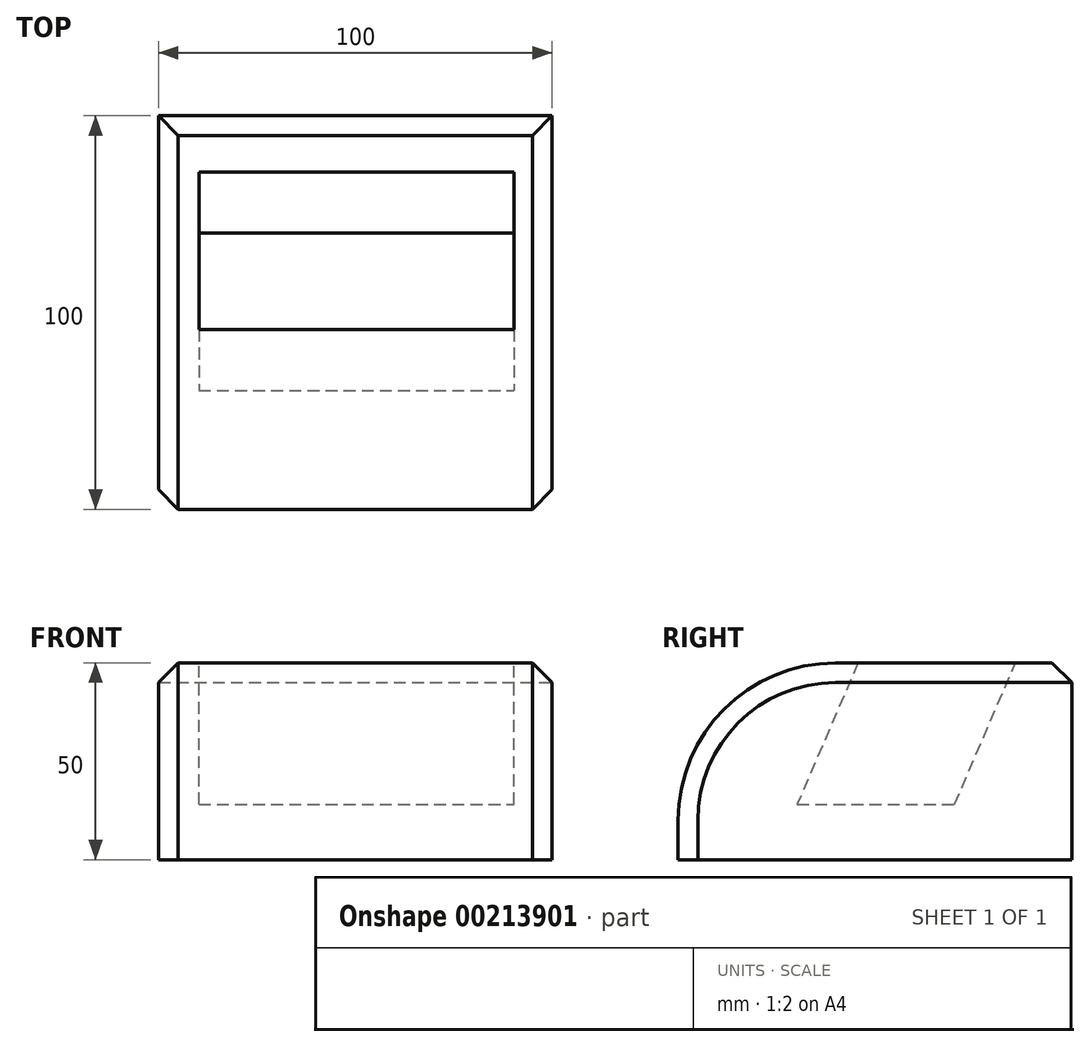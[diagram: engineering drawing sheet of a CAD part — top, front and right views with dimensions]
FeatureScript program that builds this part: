
annotation { "Feature Type Name" : "Feature", "Feature Type Description" : "" }
export const myFeature = defineFeature(function(context is Context, id is Id, definition is map)
    precondition{}
    {
        {
            var Q0;
            Q0=qCreatedBy(makeId("Front.planeOp"),FACE);
            var sketch = newSketch(context, id + "F0", { "sketchPlane" : qUnion([Q0])});
            skLineSegment(sketch, "E0.bottom", {"start": v(-50.24, 0.51) * mm, "end": v(49.76, 0.51) * mm});
            skLineSegment(sketch, "E0.top", {"start": v(-50.24, -49.49) * mm, "end": v(49.76, -49.49) * mm});
            skLineSegment(sketch, "E0.left", {"start": v(-50.24, 0.51) * mm, "end": v(-50.24, -49.49) * mm});
            skLineSegment(sketch, "E0.right", {"start": v(49.76, 0.51) * mm, "end": v(49.76, -49.49) * mm});
            skSolve(sketch);
        }
        {
            var Q0;
            Q0 = qSketchRegion(id + "F0", true);
            extrude(context, id + "F1", {"entities" : qUnion([Q0]), "endBound" : BoundingType.SYMMETRIC, "depth" : 100 * mm});
        }
        {
            var Q0;
            Q0=qCreatedBy(makeId("Right.planeOp"),FACE);
            var sketch = newSketch(context, id + "F2", { "sketchPlane" : qUnion([Q0])});
            skLineSegment(sketch, "E1", {"start": v(40, 10.51) * mm, "end": v(0, 10.51) * mm});
            skLineSegment(sketch, "E2", {"start": v(0, 10.51) * mm, "end": v(-19.77, -35.41) * mm});
            skLineSegment(sketch, "E3", {"start": v(-19.77, -35.41) * mm, "end": v(20.23, -35.41) * mm});
            skLineSegment(sketch, "E4", {"start": v(20.23, -35.41) * mm, "end": v(40, 10.51) * mm});
            skSolve(sketch);
        }
        {
            var Q0;
            Q0 = qSketchRegion(id + "F2", true);
            extrude(context, id + "F3", {"entities" : qUnion([Q0]), "operationType" : NewBodyOperationType.REMOVE, "endBound" : BoundingType.SYMMETRIC, "oppositeDirection" : true, "depth" : 80 * mm});
        }
        {
            var Q0;
            Q0=makeQuery(id+"F1.opExtrude","CAP_EDGE",EDGE,{"disambiguationData":[OSD([sQuery(id+"F0.wireOp",EDGE,"E0.bottom")])],"isStart":false});
            fillet(context, id + "F4", {"entities" : qUnion([Q0]), "radius" : 40 * mm, "tangentPropagation" : true, "allowEdgeOverflow" : false});
        }
        {
            var Q0;
            Q0=makeQuery(id+"F1.opExtrude","SWEPT_EDGE",EDGE,{"disambiguationData":[OSD([sQuery(id+"F0.wireOp",EDGE,"E0.bottom"),sQuery(id+"F0.wireOp",EDGE,"E0.left")])]});
            chamfer(context, id + "F5", {"entities" : qUnion([Q0]), "width" : 5 * mm, "tangentPropagation" : true});
        }
        {
            var Q0;
            Q0=makeQuery(id+"F1.opExtrude","SWEPT_EDGE",EDGE,{"disambiguationData":[OSD([sQuery(id+"F0.wireOp",EDGE,"E0.bottom"),sQuery(id+"F0.wireOp",EDGE,"E0.right")])]});
            chamfer(context, id + "F6", {"entities" : qUnion([Q0]), "width" : 5 * mm, "tangentPropagation" : true});
        }
        {
            var Q0;
            Q0=makeQuery(id+"F1.opExtrude","CAP_EDGE",EDGE,{"disambiguationData":[OSD([sQuery(id+"F0.wireOp",EDGE,"E0.bottom")])],"isStart":true});
            chamfer(context, id + "F7", {"entities" : qUnion([Q0]), "width" : 5 * mm, "tangentPropagation" : true});
        }
    });
